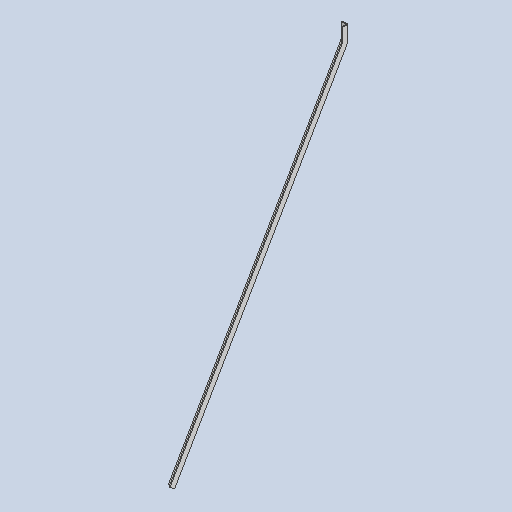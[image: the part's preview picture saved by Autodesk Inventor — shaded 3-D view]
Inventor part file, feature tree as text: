
AUTODESK INVENTOR PART (.ipt)
format: ipt  version: 2023 (Build 270158030, 158C)  size: 101,376 bytes
history: native  units: in
note: dims shown in document units (in); Inventor stores cm internally (conversion verified against a paired STEP export)
features: extrude x2, sketch x1
ambient origin geometry x8: Origin, YZ Plane, XZ Plane, XY Plane, X Axis, Y Axis, Z Axis, Center Point
bodies: Solid1 (feature_tree)
feature tree (3):
  sketch  "Sketch1"  dims[d0=45.0in d1=0.75in d2=45.0in d3=30.0deg d4=2.0in d5=0.75in d6=0.125in d7=45.0in d8=0.125in d9=0.125in d10=0.0in d11=0.625in d12=0.0in]
  extrude  "Extrusion1"  Depth=0.75in
  extrude  "Extrusion2"  Depth=45.0in
